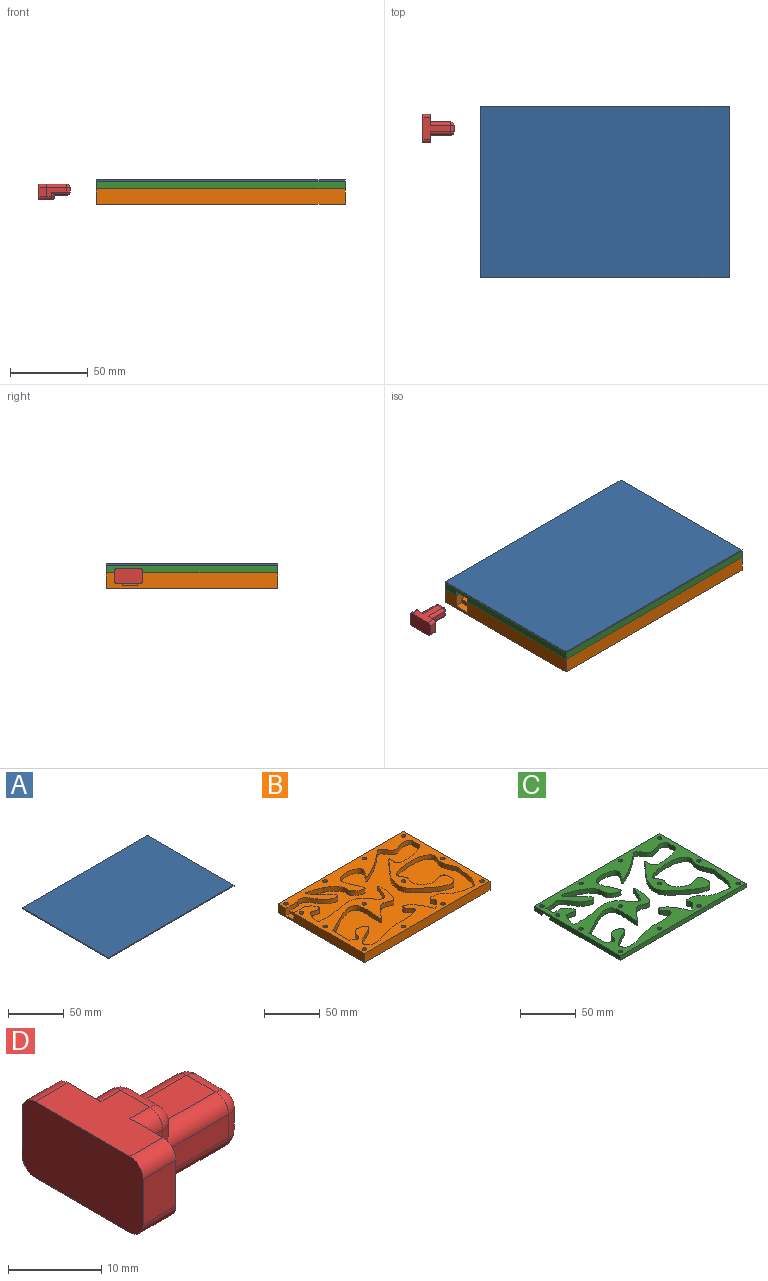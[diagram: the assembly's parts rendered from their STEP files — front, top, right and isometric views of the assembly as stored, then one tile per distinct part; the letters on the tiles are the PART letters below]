
ASSEMBLY  parts=4 mates=4
PART A: 6 faces, bbox 160x110x1 mm
  f0: plane 160x1mm, normal (0,1,0), area 160mm2, adj f1,f3,f4,f5
  f1: plane 110x1mm, normal (-1,0,0), area 110mm2, adj f0,f2,f4,f5
  f2: plane 160x1mm, normal (0,-1,0), area 160mm2, adj f1,f3,f4,f5
  f3: plane 110x1mm, normal (1,0,0), area 110mm2, adj f0,f2,f4,f5
  f4: plane 160x110mm, normal (0,0,1), area 17600mm2, adj f0,f1,f2,f3
  f5: plane 160x110mm, normal (0,0,-1), area 17600mm2, adj f0,f1,f2,f3
PART B: 36 faces, bbox 160x111.2x10 mm
  f0: plane 15x8mm, normal (0,-1,0), area 90mm2, adj f1,f18,f20,f22,f32,f35
  f1: plane 10x3mm, normal (-1,0,0), area 30mm2, adj f0,f2,f20,f22
  f2: plane 15x8mm, normal (0,1,0), area 90mm2, adj f1,f18,f20,f22,f31,f35
  f3: plane 160x10mm, normal (0,-1,0), area 1600mm2, adj f4,f18,f21,f35
  f4: plane 110x10mm, normal (1,0,0), area 1100mm2, adj f3,f5,f21,f35
  f5: plane 160x10mm, normal (0,1,0), area 1600mm2, adj f4,f18,f21,f35
  f6: cylinder r=2mm len=10mm, axis (0,0,-1), area 125.7mm2, adj f21,f35
  f7: cylinder r=2mm len=10mm, axis (0,0,-1), area 125.7mm2, adj f21,f35
  f8: cylinder r=2mm len=10mm, axis (0,0,-1), area 125.7mm2, adj f21,f35
  f9: cylinder r=2mm len=10mm, axis (0,0,-1), area 125.7mm2, adj f21,f35
  f10: cylinder r=2mm len=10mm, axis (0,0,-1), area 125.7mm2, adj f21,f35
  f11: cylinder r=2mm len=10mm, axis (0,0,-1), area 125.7mm2, adj f21,f35
  f12: cylinder r=2mm len=10mm, axis (0,0,-1), area 125.7mm2, adj f21,f35
  f13: cylinder r=2mm len=10mm, axis (0,0,-1), area 125.7mm2, adj f21,f35
  f14: cylinder r=2mm len=10mm, axis (0,0,-1), area 125.7mm2, adj f21,f35
  f15: cylinder r=2mm len=10mm, axis (0,0,-1), area 125.7mm2, adj f21,f35
  f16: cylinder r=2mm len=10mm, axis (0,0,-1), area 125.7mm2, adj f21,f35
  f17: cylinder r=2mm len=10mm, axis (0,0,-1), area 125.7mm2, adj f21,f35
  f18: plane 110x10mm, normal (-1,0,0), area 1020mm2, adj f0,f2,f3,f5,f21,f22,f35
  f19: cylinder r=2mm len=10mm, axis (0,0,-1), area 125.7mm2, adj f21,f35
  f20: plane 155.87x106.24mm, normal (0,0,1), area 9895.2mm2, adj f0,f1,f2,f23,f24,f25,f26,f27
  f21: plane 160x110mm, normal (0,0,-1), area 17436.6mm2, adj f3,f4,f5,f6,f7,f8,f9,f10
  f22: plane 10x5mm, normal (0,0,1), area 50mm2, adj f0,f1,f2,f18
  f23: extruded ~65.15x57.83mm, area 1476.6mm2, adj f20,f24,f34,f35
  f24: extruded ~30x10mm, area 161.5mm2, adj f20,f23,f25,f35
  f25: extruded ~50x14.69mm, area 328mm2, adj f20,f24,f26,f35
  f26: extruded ~70x22.73mm, area 508.1mm2, adj f20,f25,f27,f35
  f27: plane 10x5mm, normal (0,1,0), area 50mm2, adj f20,f26,f28,f35
  f28: extruded ~27.09x27.01mm, area 365.7mm2, adj f20,f27,f29,f35
  f29: plane 20x5mm, normal (1,0,0), area 100mm2, adj f20,f28,f30,f35
  f30: extruded ~78.9x39.06mm, area 1219.6mm2, adj f20,f29,f31,f35
  f31: extruded ~25x17.43mm, area 205.6mm2, adj f2,f20,f30,f35
  f32: extruded ~32.23x24.29mm, area 452.4mm2, adj f0,f20,f33,f35
  f33: extruded ~108.36x33.74mm, area 952.5mm2, adj f20,f32,f34,f35
  f34: plane 10.01x5mm, normal (-1,0,0), area 50.1mm2, adj f20,f23,f33,f35
  f35: plane 160x111.24mm, normal (0,0,1), area 7491.4mm2, adj f0,f2,f3,f4,f5,f6,f7,f8
PART C: 35 faces, bbox 160x111.2x5 mm
  f0: plane 15x5mm, normal (0,1,0), area 65mm2, adj f10,f14,f31,f32,f33,f34
  f1: plane 15x5mm, normal (0,-1,0), area 65mm2, adj f14,f15,f31,f32,f33,f34
  f2: extruded ~65.15x57.83mm, area 1476.6mm2, adj f3,f28,f31,f32
  f3: extruded ~30x10mm, area 161.5mm2, adj f2,f4,f31,f32
  f4: extruded ~50x14.69mm, area 328mm2, adj f3,f5,f31,f32
  f5: extruded ~70x22.73mm, area 508.1mm2, adj f4,f6,f31,f32
  f6: plane 10x5mm, normal (0,1,0), area 50mm2, adj f5,f7,f31,f32
  f7: extruded ~27.09x27.01mm, area 365.7mm2, adj f6,f8,f31,f32
  f8: plane 20x5mm, normal (1,0,0), area 100mm2, adj f7,f9,f31,f32
  f9: extruded ~78.9x39.06mm, area 1219.6mm2, adj f8,f10,f31,f32
  f10: extruded ~25x17.43mm, area 205.6mm2, adj f0,f9,f31,f32
  f11: plane 160x5mm, normal (0,-1,0), area 800mm2, adj f12,f14,f31,f32
  f12: plane 110x5mm, normal (1,0,0), area 550mm2, adj f11,f13,f31,f32
  f13: plane 160x5mm, normal (0,1,0), area 800mm2, adj f12,f14,f31,f32
  f14: plane 110x5mm, normal (-1,0,0), area 520mm2, adj f0,f1,f11,f13,f31,f32,f34
  f15: extruded ~32.23x24.29mm, area 452.4mm2, adj f1,f16,f31,f32
  f16: extruded ~108.36x33.74mm, area 952.5mm2, adj f15,f28,f31,f32
  f17: cylinder r=2mm len=5mm, axis (0,0,-1), area 62.8mm2, adj f31,f32
  f18: cylinder r=2mm len=5mm, axis (0,0,-1), area 62.8mm2, adj f31,f32
  f19: cylinder r=2mm len=5mm, axis (0,0,-1), area 62.8mm2, adj f31,f32
  f20: cylinder r=2mm len=5mm, axis (0,0,-1), area 62.8mm2, adj f31,f32
  f21: cylinder r=2mm len=5mm, axis (0,0,-1), area 62.8mm2, adj f31,f32
  f22: cylinder r=2mm len=5mm, axis (0,0,-1), area 62.8mm2, adj f31,f32
  f23: cylinder r=2mm len=5mm, axis (0,0,-1), area 62.8mm2, adj f31,f32
  f24: cylinder r=2mm len=5mm, axis (0,0,-1), area 62.8mm2, adj f31,f32
  f25: cylinder r=2mm len=5mm, axis (0,0,-1), area 62.8mm2, adj f31,f32
  f26: cylinder r=2mm len=5mm, axis (0,0,-1), area 62.8mm2, adj f31,f32
  f27: cylinder r=2mm len=5mm, axis (0,0,-1), area 62.8mm2, adj f31,f32
  f28: plane 10.01x5mm, normal (-1,0,0), area 50.1mm2, adj f2,f16,f31,f32
  f29: cylinder r=2mm len=5mm, axis (0,0,-1), area 62.8mm2, adj f31,f32
  f30: cylinder r=2mm len=5mm, axis (0,0,-1), area 62.8mm2, adj f31,f32
  f31: plane 160x111.24mm, normal (0,0,1), area 7541.4mm2, adj f0,f1,f2,f3,f4,f5,f6,f7
  f32: plane 160x111.24mm, normal (0,0,-1), area 7491.4mm2, adj f0,f1,f2,f3,f4,f5,f6,f7
  f33: plane 10x2mm, normal (1,0,0), area 20mm2, adj f0,f1,f31,f34
  f34: plane 10x5mm, normal (0,0,-1), area 50mm2, adj f0,f1,f14,f33
PART D: 35 faces, bbox 20x18.4x10 mm
  f0: plane 13x6mm, normal (0,-1,0), area 48mm2, adj f7,f12,f16,f17,f18,f19
  f1: plane 4.4x3mm, normal (1,0,0), area 13.2mm2, adj f15,f16,f23,f24
  f2: plane 13x6mm, normal (0,1,0), area 48mm2, adj f3,f14,f23,f26,f29,f30
  f3: plane 10x7mm, normal (1,0,0), area 50mm2, adj f2,f4,f9,f11,f14,f26,f32,f34
  f4: plane 6x5mm, normal (0,1,0), area 30mm2, adj f3,f5,f32,f34
  f5: plane 18.4x10mm, normal (-1,0,0), area 180.6mm2, adj f4,f6,f9,f11,f31,f32,f33,f34
  f6: plane 6x5mm, normal (0,-1,0), area 30mm2, adj f5,f7,f31,f33
  f7: plane 10x7mm, normal (1,0,0), area 50mm2, adj f0,f6,f9,f11,f12,f19,f31,f33
  f8: plane 8x4.4mm, normal (0,0,1), area 35.2mm2, adj f10,f17,f24,f29
  f9: plane 18x14.4mm, normal (0,0,-1), area 129.2mm2, adj f3,f5,f7,f12,f14,f15,f33,f34
  f10: plane 4.4x1mm, normal (1,0,0), area 4.4mm2, adj f8,f18,f25,f30
  f11: plane 14.4x8mm, normal (0,0,1), area 85.2mm2, adj f3,f5,f7,f19,f25,f26,f31,f32
  f12: cylinder r=2mm len=13mm, axis (1,0,0), area 40.8mm2, adj f0,f7,f9,f13
  f13: sphere r=2mm, area 6.3mm2, adj f12,f15,f16
  f14: cylinder r=2mm len=13mm, axis (-1,0,0), area 40.8mm2, adj f2,f3,f9,f20
  f15: cylinder r=2mm len=4.4mm, axis (0,1,0), area 13.8mm2, adj f1,f9,f13,f20
  f16: cylinder r=2mm len=3mm, axis (0,0,-1), area 9.4mm2, adj f0,f1,f13,f21
  f17: cylinder r=2mm len=10mm, axis (-1,0,0), area 27.4mm2, adj f0,f8,f18,f21
  f18: cylinder r=2mm len=3mm, axis (0,0,1), area 5.4mm2, adj f0,f10,f17,f22
  f19: cylinder r=2mm len=3mm, axis (-1,0,0), area 9.4mm2, adj f0,f7,f11,f22
  f20: sphere r=2mm, area 6.3mm2, adj f14,f15,f23
  f21: sphere r=2mm, area 6.3mm2, adj f16,f17,f24
  f22: sphere r=2mm, area 6.3mm2, adj f18,f19,f25
  f23: cylinder r=2mm len=3mm, axis (0,0,-1), area 9.4mm2, adj f1,f2,f20,f27
  f24: cylinder r=2mm len=4.4mm, axis (0,-1,0), area 13.8mm2, adj f1,f8,f21,f27
  f25: cylinder r=2mm len=4.4mm, axis (0,-1,0), area 13.8mm2, adj f10,f11,f22,f28
  f26: cylinder r=2mm len=3mm, axis (1,0,0), area 9.4mm2, adj f2,f3,f11,f28
  f27: sphere r=2mm, area 6.3mm2, adj f23,f24,f29
  f28: sphere r=2mm, area 6.3mm2, adj f25,f26,f30
  f29: cylinder r=2mm len=10mm, axis (1,0,0), area 27.4mm2, adj f2,f8,f27,f30
  f30: cylinder r=2mm len=3mm, axis (0,0,1), area 5.4mm2, adj f2,f10,f28,f29
  f31: cylinder r=2mm len=5mm, axis (-1,0,0), area 15.7mm2, adj f5,f6,f7,f11
  f32: cylinder r=2mm len=5mm, axis (1,0,0), area 15.7mm2, adj f3,f4,f5,f11
  f33: cylinder r=2mm len=5mm, axis (1,0,0), area 15.7mm2, adj f5,f6,f7,f9
  f34: cylinder r=2mm len=5mm, axis (-1,0,0), area 15.7mm2, adj f3,f4,f5,f9
PLACE A t=(5,5,-15)mm
PLACE B t=(5,5,0)mm
PLACE C t=(5,5,-10)mm
PLACE D rot(axis=(1,0,0),180deg) t=(-1.84,185.8,13)mm
MATE planar D.f9 <-> C.f34  axis (0,0,1) through (-18.84,95.8,13)mm
MATE fastened A.f5 <-> C.f31  axis (0,0,-1) through (0,110,15)mm
MATE planar B.f0 <-> D.f0  axis (0,-1,0) through (0,100,6)mm
MATE fastened C.f32 <-> B.f35  axis (0,0,1) through (0,0,10)mm
